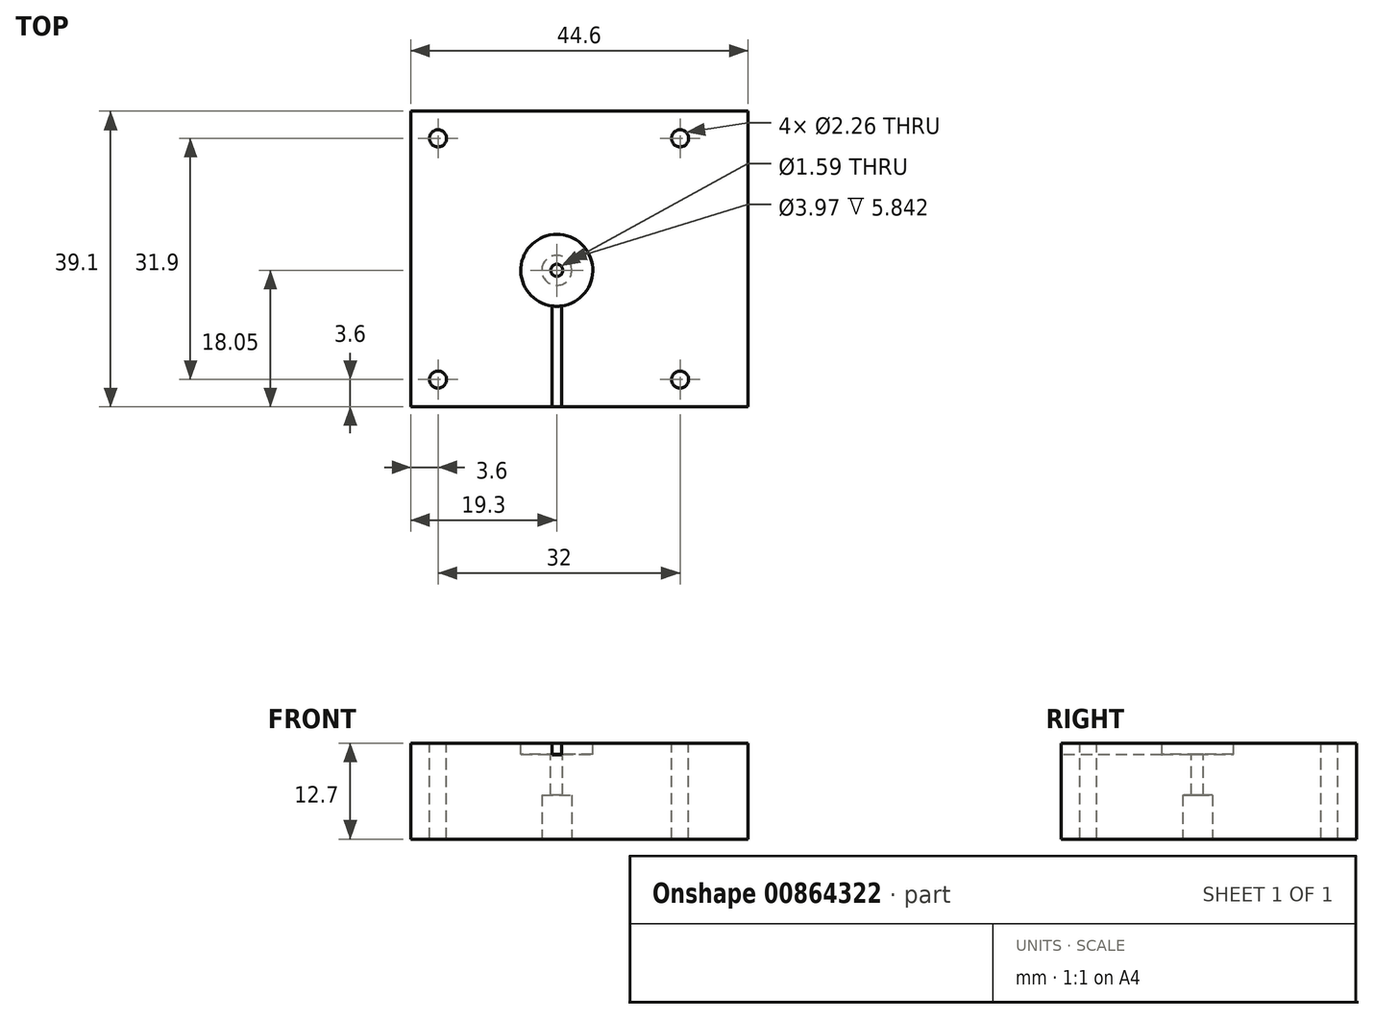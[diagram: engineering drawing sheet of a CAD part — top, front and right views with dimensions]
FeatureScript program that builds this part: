
annotation { "Feature Type Name" : "Feature", "Feature Type Description" : "" }
export const myFeature = defineFeature(function(context is Context, id is Id, definition is map)
    precondition{}
    {
        {
            var Q0;
            Q0=qCreatedBy(makeId("Top.planeOp"),FACE);
            var sketch = newSketch(context, id + "F0", { "sketchPlane" : qUnion([Q0])});
            skLineSegment(sketch, "E0.bottom", {"start": v(0, 0) * mm, "end": v(44.6, 0) * mm});
            skLineSegment(sketch, "E0.top", {"start": v(0, 39.1) * mm, "end": v(44.6, 39.1) * mm});
            skLineSegment(sketch, "E0.left", {"start": v(0, 0) * mm, "end": v(0, 39.1) * mm});
            skLineSegment(sketch, "E0.right", {"start": v(44.6, 0) * mm, "end": v(44.6, 39.1) * mm});
            skSolve(sketch);
        }
        {
            var Q0;
            Q0=makeQuery(id+"F0.imprint","IMPRINT",FACE,{"disambiguationData":[TD([[makeQuery(id+"F0.imprint","IMPRINT",EDGE,{"derivedFrom":sQuery(id+"F0.wireOp",EDGE,"E0.bottom")}),1.0]])]});
            extrude(context, id + "F1", {"entities" : qUnion([Q0]), "depth" : 12.7 * mm, "offsetDistance" : 25.4 * mm});
        }
        {
            var Q0;
            Q0=makeQuery(id+"F1.opExtrude","CAP_FACE",FACE,{"disambiguationData":[OSD([sQuery(id+"F0.wireOp",EDGE,"E0.bottom"),sQuery(id+"F0.wireOp",EDGE,"E0.top"),sQuery(id+"F0.wireOp",EDGE,"E0.left"),sQuery(id+"F0.wireOp",EDGE,"E0.right")])],"isStart":false});
            var sketch = newSketch(context, id + "F2", { "sketchPlane" : qUnion([Q0])});
            skCircle(sketch, "E1", {"center": v(3.6, 35.5) * mm, "radius": 1.13 * mm});
            skCircle(sketch, "E2", {"center": v(35.6, 35.5) * mm, "radius": 1.13 * mm});
            skCircle(sketch, "E3", {"center": v(35.6, 3.6) * mm, "radius": 1.13 * mm});
            skCircle(sketch, "E4", {"center": v(3.6, 3.6) * mm, "radius": 1.13 * mm});
            skSolve(sketch);
        }
        {
            var Q0;
            Q0=makeQuery(id+"F2.imprint","IMPRINT",FACE,{"disambiguationData":[TD([[makeQuery(id+"F2.imprint","IMPRINT",EDGE,{"derivedFrom":sQuery(id+"F2.wireOp",EDGE,"E1")}),1.0]])]});
            var Q1;
            Q1=makeQuery(id+"F2.imprint","IMPRINT",FACE,{"disambiguationData":[TD([[makeQuery(id+"F2.imprint","IMPRINT",EDGE,{"derivedFrom":sQuery(id+"F2.wireOp",EDGE,"E4")}),1.0]])]});
            var Q2;
            Q2=makeQuery(id+"F2.imprint","IMPRINT",FACE,{"disambiguationData":[TD([[makeQuery(id+"F2.imprint","IMPRINT",EDGE,{"derivedFrom":sQuery(id+"F2.wireOp",EDGE,"E3")}),1.0]])]});
            var Q3;
            Q3=makeQuery(id+"F2.imprint","IMPRINT",FACE,{"disambiguationData":[TD([[makeQuery(id+"F2.imprint","IMPRINT",EDGE,{"derivedFrom":sQuery(id+"F2.wireOp",EDGE,"E2")}),1.0]])]});
            extrude(context, id + "F3", {"entities" : qUnion([Q0, Q1, Q2, Q3]), "operationType" : NewBodyOperationType.REMOVE, "oppositeDirection" : true, "depth" : 25 * mm, "offsetDistance" : 25 * mm});
        }
        {
            var Q0;
            Q0=makeQuery(id+"F1.opExtrude","CAP_FACE",FACE,{"disambiguationData":[OSD([sQuery(id+"F0.wireOp",EDGE,"E0.bottom"),sQuery(id+"F0.wireOp",EDGE,"E0.top"),sQuery(id+"F0.wireOp",EDGE,"E0.left"),sQuery(id+"F0.wireOp",EDGE,"E0.right")])],"isStart":false});
            var sketch = newSketch(context, id + "F4", { "sketchPlane" : qUnion([Q0])});
            skLineSegment(sketch, "E5", {"start": v(3.6, 35.5) * mm, "end": v(35.6, 3.6) * mm, "construction": true});
            skLineSegment(sketch, "E6", {"start": v(3.6, 3.6) * mm, "end": v(35.6, 35.5) * mm, "construction": true});
            skCircle(sketch, "E7", {"center": v(19.3, 18.05) * mm, "radius": 4.76 * mm});
            skPoint(sketch, "E8", {"position": v(19.6, 19.55) * mm});
            skSolve(sketch);
        }
        {
            var Q0;
            Q0=makeQuery(id+"F4.imprint","IMPRINT",FACE,{"disambiguationData":[TD([[makeQuery(id+"F4.imprint","IMPRINT",EDGE,{"derivedFrom":sQuery(id+"F4.wireOp",EDGE,"E7")}),1.0]])]});
            extrude(context, id + "F5", {"entities" : qUnion([Q0]), "operationType" : NewBodyOperationType.REMOVE, "oppositeDirection" : true, "depth" : 1.5 * mm, "offsetDistance" : 25 * mm});
        }
        {
            var Q0;
            Q0=makeQuery(id+"F5.boolean.opBoolean","COPY",FACE,{"derivedFrom":makeQuery(id+"F5.opExtrude","CAP_FACE",FACE,{"disambiguationData":[OSD([sQuery(id+"F4.wireOp",EDGE,"E7")])],"isStart":false})});
            var sketch = newSketch(context, id + "F6", { "sketchPlane" : qUnion([Q0])});
            skCircle(sketch, "E9", {"center": v(19.3, 18.05) * mm, "radius": 0.8 * mm});
            skSolve(sketch);
        }
        {
            var Q0;
            Q0=makeQuery(id+"F6.imprint","IMPRINT",FACE,{"disambiguationData":[TD([[makeQuery(id+"F6.imprint","IMPRINT",EDGE,{"derivedFrom":sQuery(id+"F6.wireOp",EDGE,"E9")}),1.0]])]});
            extrude(context, id + "F7", {"entities" : qUnion([Q0]), "operationType" : NewBodyOperationType.REMOVE, "endBound" : BoundingType.UP_TO_NEXT, "oppositeDirection" : true, "depth" : 25.4 * mm, "offsetDistance" : 25.4 * mm});
        }
        {
            var Q0;
            Q0=makeQuery(id+"F1.opExtrude","CAP_FACE",FACE,{"disambiguationData":[OSD([sQuery(id+"F0.wireOp",EDGE,"E0.bottom"),sQuery(id+"F0.wireOp",EDGE,"E0.top"),sQuery(id+"F0.wireOp",EDGE,"E0.left"),sQuery(id+"F0.wireOp",EDGE,"E0.right")])],"isStart":true});
            var sketch = newSketch(context, id + "F8", { "sketchPlane" : qUnion([Q0])});
            skCircle(sketch, "E10", {"center": v(19.3, -18.05) * mm, "radius": 1.98 * mm});
            skSolve(sketch);
        }
        {
            var Q0;
            Q0=makeQuery(id+"F8.imprint","IMPRINT",FACE,{"disambiguationData":[TD([[makeQuery(id+"F8.imprint","IMPRINT",EDGE,{"derivedFrom":sQuery(id+"F8.wireOp",EDGE,"E10")}),1.0]])]});
            var Q1;
            Q1=sQuery(id+"F8.wireOp",EDGE,"E10");
            extrude(context, id + "F9", {"entities" : qUnion([Q0]), "operationType" : NewBodyOperationType.REMOVE, "surfaceEntities" : qUnion([Q1]), "oppositeDirection" : true, "depth" : 5.84 * mm, "offsetDistance" : 25.4 * mm});
        }
        {
            var Q0;
            Q0=makeQuery(id+"F1.opExtrude","CAP_FACE",FACE,{"disambiguationData":[OSD([sQuery(id+"F0.wireOp",EDGE,"E0.bottom"),sQuery(id+"F0.wireOp",EDGE,"E0.top"),sQuery(id+"F0.wireOp",EDGE,"E0.left"),sQuery(id+"F0.wireOp",EDGE,"E0.right")])],"isStart":false});
            var sketch = newSketch(context, id + "F10", { "sketchPlane" : qUnion([Q0])});
            skLineSegment(sketch, "E11.bottom", {"start": v(18.67, 15.24) * mm, "end": v(19.94, 15.24) * mm});
            skLineSegment(sketch, "E11.top", {"start": v(18.67, 0) * mm, "end": v(19.94, 0) * mm});
            skLineSegment(sketch, "E11.left", {"start": v(18.67, 15.24) * mm, "end": v(18.67, 0) * mm});
            skLineSegment(sketch, "E11.right", {"start": v(19.94, 15.24) * mm, "end": v(19.94, 0) * mm});
            skSolve(sketch);
        }
        {
            var Q0;
            {var subQ0=sQuery(id+"F10.wireOp",EDGE,"E11.top");Q0=makeQuery(id+"F10.imprint","IMPRINT",FACE,{"disambiguationData":[TD([[makeQuery(id+"F10.imprint","IMPRINT",EDGE,{"derivedFrom":subQ0}),1.0]])]});}
            extrude(context, id + "F11", {"entities" : qUnion([Q0]), "operationType" : NewBodyOperationType.REMOVE, "oppositeDirection" : true, "depth" : 1.52 * mm, "offsetDistance" : 25.4 * mm});
        }
    });
